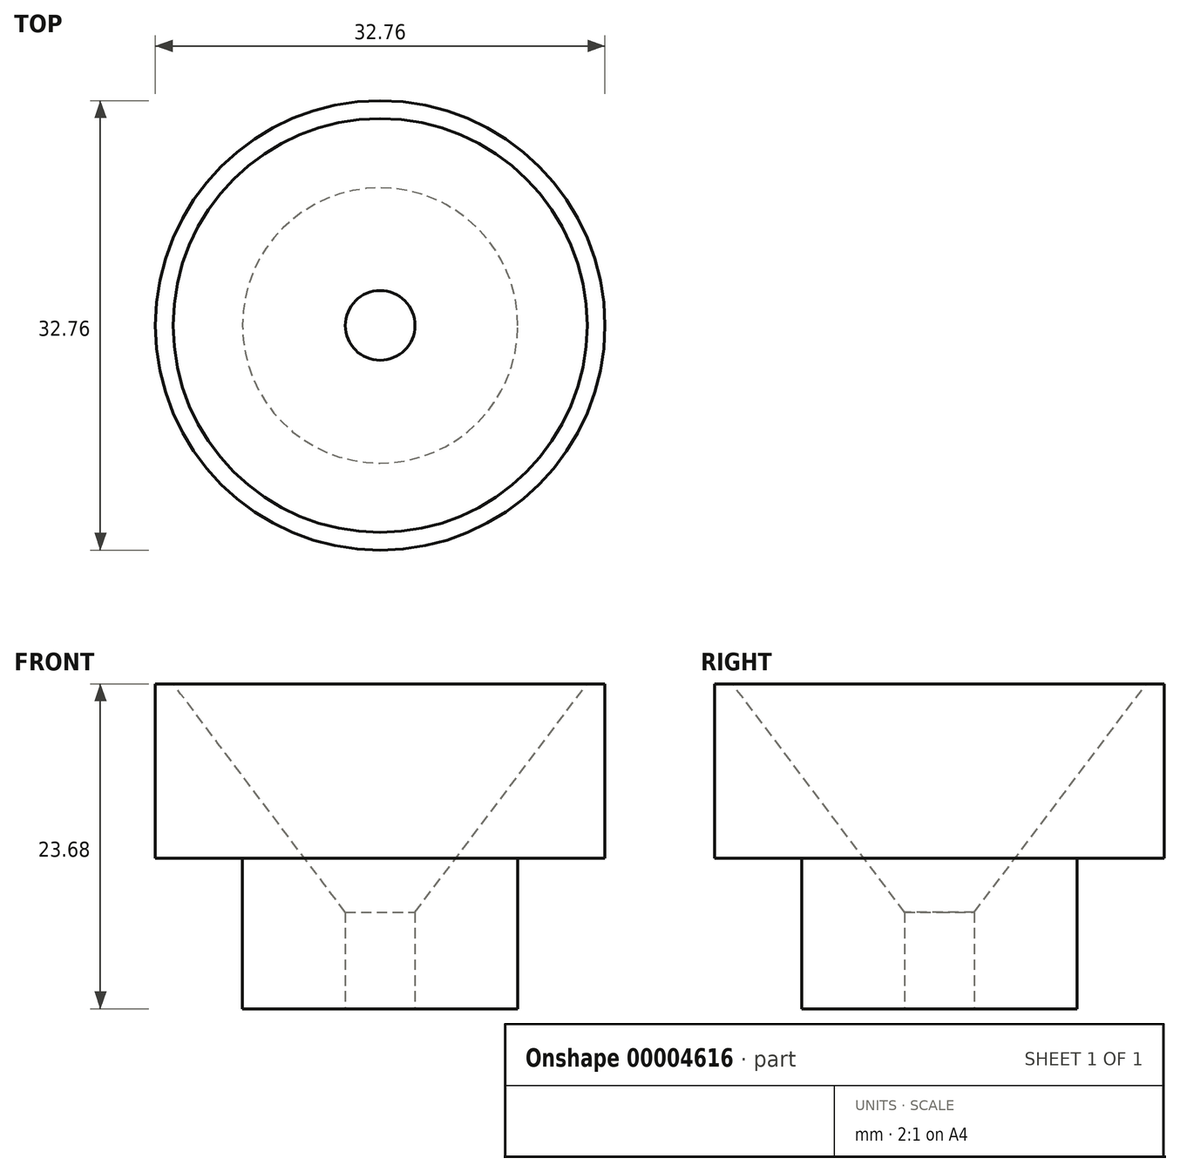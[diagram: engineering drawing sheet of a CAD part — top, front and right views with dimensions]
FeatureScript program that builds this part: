
annotation { "Feature Type Name" : "Feature", "Feature Type Description" : "" }
export const myFeature = defineFeature(function(context is Context, id is Id, definition is map)
    precondition{}
    {
        {
            var Q0;
            Q0=qCreatedBy(makeId("Front.planeOp"),FACE);
            var sketch = newSketch(context, id + "F0", { "sketchPlane" : qUnion([Q0])});
            skLineSegment(sketch, "E0", {"start": v(2.54, 0) * mm, "end": v(15.09, 16.65) * mm});
            skLineSegment(sketch, "E1", {"start": v(15.09, 16.65) * mm, "end": v(16.38, 16.65) * mm});
            skLineSegment(sketch, "E2", {"start": v(16.38, 16.65) * mm, "end": v(16.38, 3.95) * mm});
            skLineSegment(sketch, "E3", {"start": v(16.38, 3.95) * mm, "end": v(10.03, 3.95) * mm});
            skLineSegment(sketch, "E4", {"start": v(10.03, 3.95) * mm, "end": v(10.03, -7.03) * mm});
            skLineSegment(sketch, "E5", {"start": v(2.54, 0) * mm, "end": v(2.54, -7.03) * mm});
            skLineSegment(sketch, "E6", {"start": v(2.54, -7.03) * mm, "end": v(10.03, -7.03) * mm});
            skLineSegment(sketch, "E7", {"start": v(0, 0) * mm, "end": v(0, 15.62) * mm, "construction": true});
            skSolve(sketch);
        }
        {
            var Q0;
            Q0 = qSketchRegion(id + "F0", true);
            var Q1;
            Q1=sQuery(id+"F0.wireOp",EDGE,"E7");
            revolve(context, id + "F1", {"entities" : qUnion([Q0]), "axis" : qUnion([Q1]), "revolveType" : RevolveType.FULL});
        }
    });
